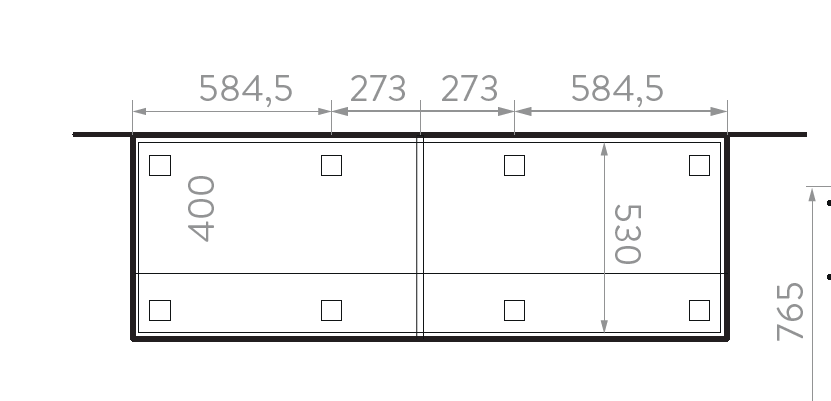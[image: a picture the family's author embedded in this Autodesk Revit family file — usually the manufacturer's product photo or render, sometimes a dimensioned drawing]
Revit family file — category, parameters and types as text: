
# Revit family: O22401711 Cocina Soho derecha
name_source: partatom
category: Generic Models
units: mm (PartAtom-declared; Revit-internal decimal feet)

## family parameters
Always vertical = Yes
Can host rebar = No
Cut with Voids When Loaded = No
Host = Wall
OmniClass Number = 23.21.23.23.13
OmniClass Title = Residential Food Cookers
Part Type = Normal
Room Calculation Point = No
Round Connector Dimension = Use Diameter
Shared = No

## types (1)
- Type 1
    Alto = 2120 mm
    Ancho mueble inferior = 1760 mm  [stored 5.77428 ft]
    Carga máxima Campana = 25 kg.
    Carga máxima Mueble Superior = 42 kg.
    Carga máxima mueble inferior = 73 kg.
    Description = Esta cocina de diseño contemporáneo está disponible en color miel, contrastado con detalles en gris plomo. Sus puertas lisas (sin manijas expuestas) aportan limpieza y continuidad al diseño, haciendo que la cocina sea más amigable con el usuario. Esta cocina entrega una solución completa al incluir en su mueble inferior un mesón en CoronaStone® con lavaplatos y cubierta con 4 fogones integrados, además de accesorios como vajillero y cubertero para hacer más cómodo el almacenamiento.En todo el mueble, los cantos o recubrimiento de bordes, cuentan con mayor espesor y rigidez al estándar del mercado, brindando un acabado estético superior y mayor protección a posibles filtraciones de humedad.Disfruta de su máximo almacenamiento y comodidad de uso, y de nuestros muebles altamente resistentes. ¡Una solución integral de fácil instalación!
    Dimensiones generales del mueble inferior (H*W*L) = 920x 1800x 600mm.
    Dimensiones generales mueble rior (H*W*L). = 650 x 345 x 1800 mm.
    Garantia Mesón = 10 años
    Garantía de Herrajes = 1 año
    Garantía de madera = 1 año
    Material Patas = Corona_Acero inoxidable
    Material meson = Corona_Cuarzo_Natural
    Material mueble inferior = Corona_Madera_Blanco
    Material mueble superior = Corona_Madera_Blanco
    Material puertas A = Corona_Madera_Aglomerada_Miel
    Material puertas B = Corona_Madera_Aglomerada_Plomo
    Peso Neto aproximado mueble inferior = 63 kg.
    Peso Neto aproximado mueble superior = 41,29 kg.
    Profundidad mueble inferior = 595 mm  [stored 1.9521 ft]
    Resistencia a la humedad = Hinchamiento < o =8%.
    URL = https://corona.co

note: [stored X ft] marks values corroborated as IEEE doubles in the binary element streams (Revit-internal decimal feet)

## geometry (parser evidence)
native form markers: Sweep x11
no freeform markers — native parametric forms only
